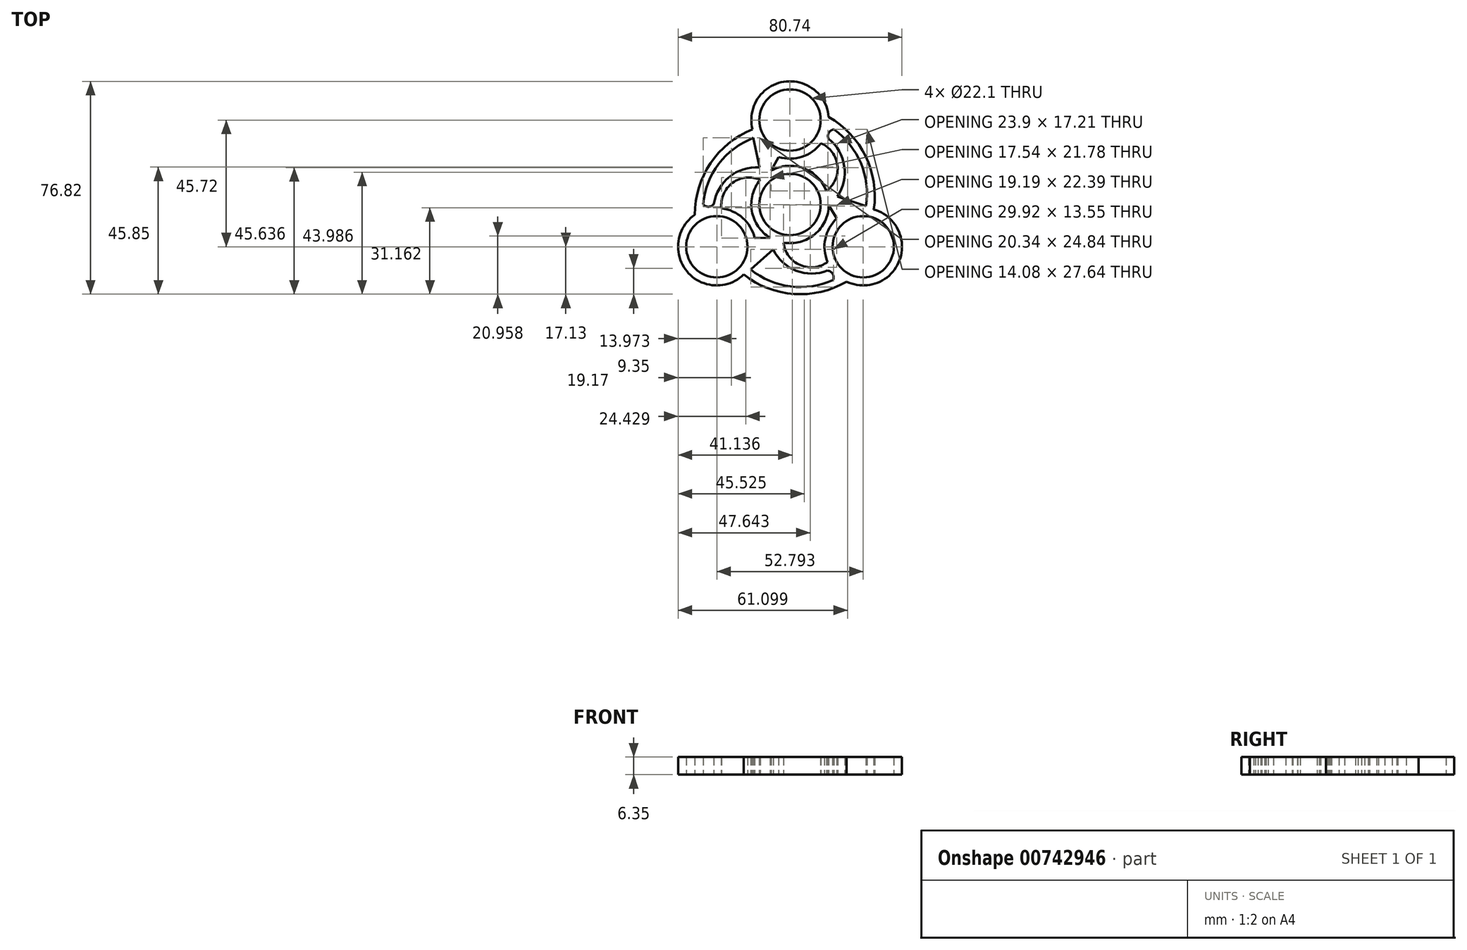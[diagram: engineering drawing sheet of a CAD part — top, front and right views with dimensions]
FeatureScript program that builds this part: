
annotation { "Feature Type Name" : "Feature", "Feature Type Description" : "" }
export const myFeature = defineFeature(function(context is Context, id is Id, definition is map)
    precondition{}
    {
        {
            var Q0;
            Q0=qCreatedBy(makeId("Top.planeOp"),FACE);
            var sketch = newSketch(context, id + "F0", { "sketchPlane" : qUnion([Q0])});
            skCircle(sketch, "E0", {"center": v(0, 0) * mm, "radius": 11.05 * mm});
            skArc(sketch, "E1", {"start": v(-10.77, 8.9) * mm, "mid": v(-13.77, -2.37) * mm, "end": v(-7.17, -11.99) * mm});
            skLineSegment(sketch, "E2", {"start": v(0, 0) * mm, "end": v(0, 30.48) * mm});
            skCircle(sketch, "E3", {"center": v(0, 30.48) * mm, "radius": 11.05 * mm});
            skArc(sketch, "E4", {"start": v(-4.09, 17.12) * mm, "mid": v(4.32, 17.2) * mm, "end": v(11.17, 22.09) * mm});
            skCircle(sketch, "E5.1.0", {"center": v(-26.4, -15.24) * mm, "radius": 11.05 * mm});
            skArc(sketch, "E5.1.1", {"start": v(-12.78, -12.1) * mm, "mid": v(-17.05, -4.85) * mm, "end": v(-24.71, -1.37) * mm});
            skCircle(sketch, "E5.2.0", {"center": v(26.4, -15.24) * mm, "radius": 11.05 * mm});
            skArc(sketch, "E5.2.1", {"start": v(16.87, -5.02) * mm, "mid": v(12.73, -12.34) * mm, "end": v(13.54, -20.71) * mm});
            skArc(sketch, "E6", {"start": v(13.1, 4.87) * mm, "mid": v(17.1, 14.04) * mm, "end": v(11.17, 22.09) * mm});
            skPoint(sketch, "E7.start.orphan", {"position": v(30.22, 0) * mm});
            skArc(sketch, "E8", {"start": v(30.22, -1.8) * mm, "mid": v(27.23, 17.4) * mm, "end": v(13.93, 31.58) * mm});
            skArc(sketch, "E9.1.0", {"start": v(-10.77, 8.9) * mm, "mid": v(-20.7, 7.8) * mm, "end": v(-24.71, -1.37) * mm});
            skArc(sketch, "E9.1.1", {"start": v(-13.55, 27.07) * mm, "mid": v(-28.7, 14.88) * mm, "end": v(-34.31, -3.73) * mm});
            skArc(sketch, "E9.2.0", {"start": v(-2.32, -13.78) * mm, "mid": v(3.6, -21.83) * mm, "end": v(13.54, -20.71) * mm});
            skArc(sketch, "E9.2.1", {"start": v(-16.67, -25.27) * mm, "mid": v(1.46, -32.29) * mm, "end": v(20.39, -27.85) * mm});
            skLineSegment(sketch, "E10", {"start": v(-4.09, 17.12) * mm, "end": v(-6.8, 12.2) * mm});
            skLineSegment(sketch, "E11.1.0", {"start": v(-12.78, -12.1) * mm, "end": v(-7.17, -11.99) * mm});
            skLineSegment(sketch, "E11.2.0", {"start": v(16.87, -5.02) * mm, "end": v(13.97, -0.22) * mm});
            skArc(sketch, "E12.trimOffspring", {"start": v(13.93, 31.58) * mm, "mid": v(-2.26, 44.27) * mm, "end": v(-13.55, 27.07) * mm});
            skArc(sketch, "E13.trimOffspring", {"start": v(20.39, -27.85) * mm, "mid": v(39.47, -20.17) * mm, "end": v(30.22, -1.8) * mm});
            skArc(sketch, "E14.trimOffspring", {"start": v(-34.31, -3.73) * mm, "mid": v(-37.2, -24.1) * mm, "end": v(-16.67, -25.27) * mm});
            skArc(sketch, "E15.trimOffspring", {"start": v(-2.32, -13.78) * mm, "mid": v(8.94, -10.74) * mm, "end": v(13.97, -0.22) * mm});
            skArc(sketch, "E16.trimOffspring", {"start": v(13.1, 4.87) * mm, "mid": v(4.83, 13.1) * mm, "end": v(-6.8, 12.2) * mm});
            skArc(sketch, "E17", {"start": v(15.82, 27.09) * mm, "mid": v(14, 25.86) * mm, "end": v(13.9, 23.67) * mm});
            skArc(sketch, "E18", {"start": v(17.1, 2.87) * mm, "mid": v(19.56, 13.9) * mm, "end": v(13.9, 23.67) * mm});
            skArc(sketch, "E19", {"start": v(27.43, -0.55) * mm, "mid": v(25.54, 14.91) * mm, "end": v(15.82, 27.09) * mm});
            skLineSegment(sketch, "E20", {"start": v(17.1, 2.87) * mm, "end": v(27.43, -0.55) * mm});
            skArc(sketch, "E21.1.0", {"start": v(-31.37, 0.16) * mm, "mid": v(-29.4, -0.8) * mm, "end": v(-27.44, 0.2) * mm});
            skArc(sketch, "E21.1.1", {"start": v(-11.03, 13.38) * mm, "mid": v(-21.81, 10) * mm, "end": v(-27.44, 0.2) * mm});
            skArc(sketch, "E21.1.2", {"start": v(-13.24, 24.03) * mm, "mid": v(-25.68, 14.66) * mm, "end": v(-31.37, 0.16) * mm});
            skLineSegment(sketch, "E21.1.3", {"start": v(-11.03, 13.38) * mm, "end": v(-13.24, 24.03) * mm});
            skArc(sketch, "E21.2.0", {"start": v(15.55, -27.24) * mm, "mid": v(15.4, -25.06) * mm, "end": v(13.55, -23.87) * mm});
            skArc(sketch, "E21.2.1", {"start": v(-6.07, -16.24) * mm, "mid": v(2.25, -23.89) * mm, "end": v(13.55, -23.87) * mm});
            skArc(sketch, "E21.2.2", {"start": v(-14.2, -23.48) * mm, "mid": v(0.14, -29.57) * mm, "end": v(15.55, -27.24) * mm});
            skLineSegment(sketch, "E21.2.3", {"start": v(-6.07, -16.24) * mm, "end": v(-14.2, -23.48) * mm});
            skSolve(sketch);
        }
        {
            var Q0;
            Q0 = qSketchRegion(id + "F0", true);
            extrude(context, id + "F1", {"entities" : qUnion([Q0]), "depth" : 6.35 * mm, "offsetDistance" : 25.4 * mm});
        }
    });
